# Revit family: Tub-Single Bowl-Clark Astron 35L
name_source: partatom
category: Plumbing Fixtures
revit_build: Autodesk Revit 2014 (Build: 20140709_2115(x64)
units: mm (PartAtom-declared; Revit-internal decimal feet)

## types (2) — shared parameters
Assembly Code = D2010420
Default Elevation = 1219 mm
Depth = 244 mm
Length = 320 mm  [stored 1.04987 ft]
Manufacturer = GWA Bathrooms & Kitchens
Material_ANZRS = Metal-Stainless-Caroma
ModifiedIssue_ANZRS = 20151014.54 $
Type Comments = Clark Astron 35L Laundry Tub
URL = http://www.specify.caroma.com.au
WFU = 2
Waste = Metal-Chrome-Caroma
WasteDiameter = 60 mm  [stored 0.19685 ft]
Width = 470 mm  [stored 1.54199 ft]
zero-valued in all types: WasteOutlet_ANZRS

## per-type parameters (varying)
| type | TapHole | TapHolePosition |
| 0TH | No | 40 mm  [stored 0.131234 ft] |
| 1TH | Yes | 0 mm  [stored 0 ft] |

note: [stored X ft] marks values corroborated as IEEE doubles in the binary element streams (Revit-internal decimal feet)

## geometry (parser evidence)
native form markers: Blend x120, Sweep x1
no freeform markers — native parametric forms only
